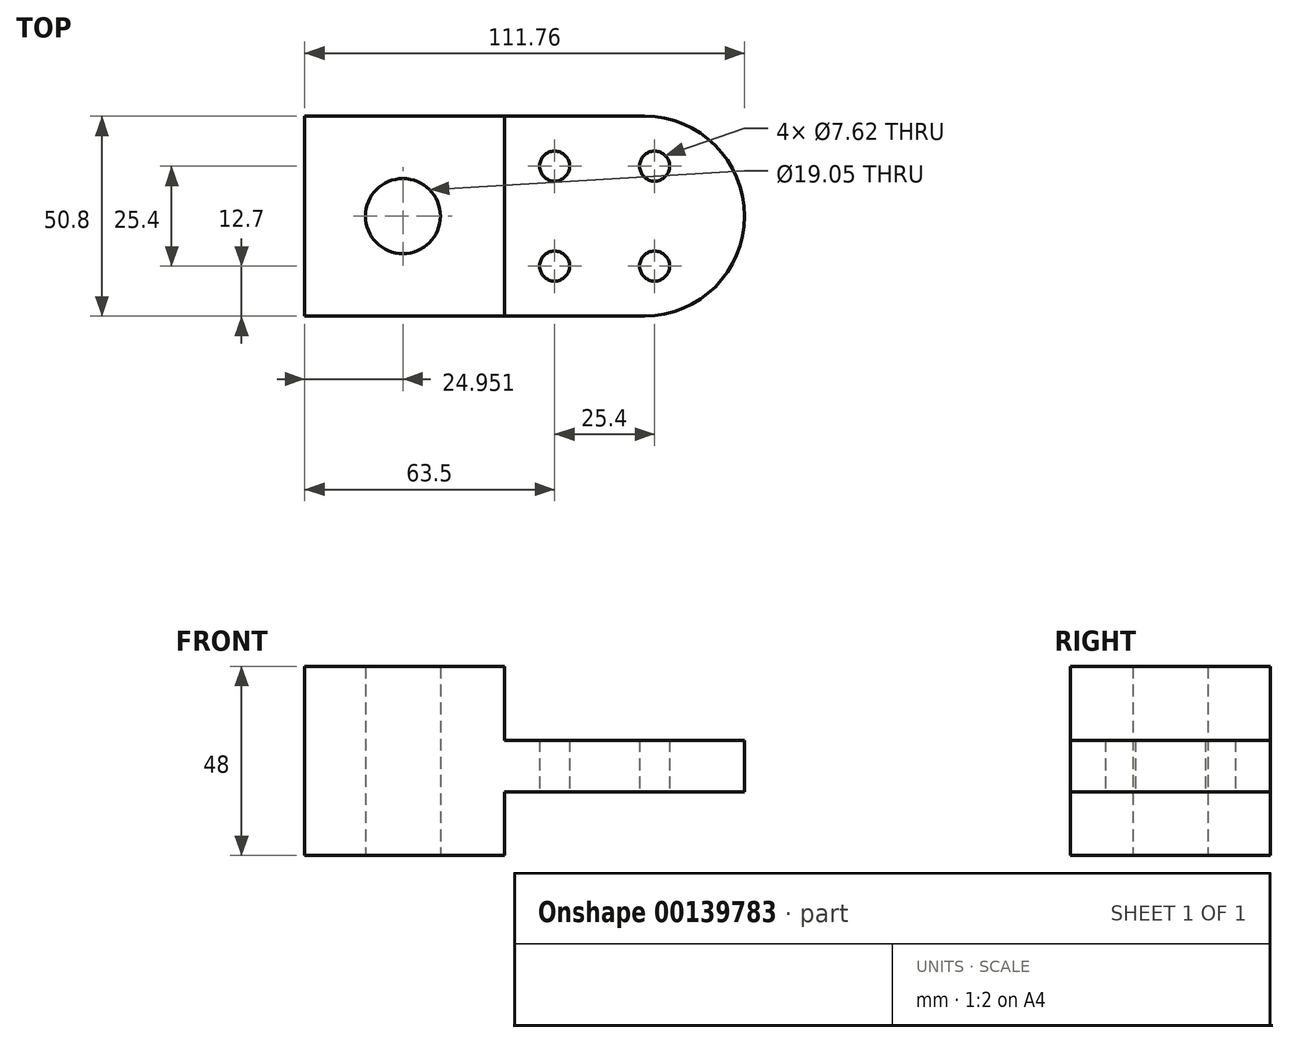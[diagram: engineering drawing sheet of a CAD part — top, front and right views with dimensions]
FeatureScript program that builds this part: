
annotation { "Feature Type Name" : "Feature", "Feature Type Description" : "" }
export const myFeature = defineFeature(function(context is Context, id is Id, definition is map)
    precondition{}
    {
        {
            var Q0;
            Q0=qCreatedBy(makeId("Front.planeOp"),FACE);
            var sketch = newSketch(context, id + "F0", { "sketchPlane" : qUnion([Q0])});
            skLineSegment(sketch, "E0", {"start": v(0, 0) * mm, "end": v(0, 48) * mm});
            skLineSegment(sketch, "E1", {"start": v(0, 48) * mm, "end": v(50.8, 48) * mm});
            skLineSegment(sketch, "E2", {"start": v(50.8, 48) * mm, "end": v(50.8, 29.23) * mm});
            skLineSegment(sketch, "E3", {"start": v(50.8, 29.23) * mm, "end": v(111.76, 29.23) * mm});
            skLineSegment(sketch, "E4", {"start": v(111.76, 29.23) * mm, "end": v(111.76, 16.07) * mm});
            skLineSegment(sketch, "E5", {"start": v(111.76, 16.07) * mm, "end": v(50.8, 16.07) * mm});
            skLineSegment(sketch, "E6", {"start": v(50.8, 16.07) * mm, "end": v(50.8, 0) * mm});
            skLineSegment(sketch, "E7", {"start": v(50.8, 0) * mm, "end": v(0, 0) * mm});
            skSolve(sketch);
        }
        {
            var Q0;
            Q0 = qSketchRegion(id + "F0", true);
            extrude(context, id + "F1", {"entities" : qUnion([Q0]), "depth" : 50.8 * mm});
        }
        {
            var Q0;
            Q0=qCreatedBy(makeId("Top.planeOp"),FACE);
            var sketch = newSketch(context, id + "F2", { "sketchPlane" : qUnion([Q0])});
            skPoint(sketch, "E8", {"position": v(24.95, -25.4) * mm});
            skCircle(sketch, "E9", {"center": v(63.5, -12.7) * mm, "radius": 3.81 * mm});
            skCircle(sketch, "E10.0.1.0", {"center": v(63.5, -38.1) * mm, "radius": 3.81 * mm});
            skLineSegment(sketch, "E10.direction1", {"start": v(63.5, -12.7) * mm, "end": v(88.9, -12.7) * mm, "construction": true});
            skLineSegment(sketch, "E10.direction2", {"start": v(63.5, -12.7) * mm, "end": v(63.5, -38.1) * mm, "construction": true});
            skCircle(sketch, "E11.0.1.0", {"center": v(88.9, -12.7) * mm, "radius": 3.81 * mm});
            skCircle(sketch, "E11.0.1.1", {"center": v(88.9, -38.1) * mm, "radius": 3.81 * mm});
            skLineSegment(sketch, "E12", {"start": v(86.36, 0) * mm, "end": v(88.9, 0) * mm});
            skLineSegment(sketch, "E13", {"start": v(111.76, -25.4) * mm, "end": v(111.76, -25.4) * mm});
            skLineSegment(sketch, "E14", {"start": v(88.9, -50.8) * mm, "end": v(86.36, -50.8) * mm});
            skPoint(sketch, "E15.visualSharp", {"position": v(111.76, 0) * mm});
            skArc(sketch, "E15.filletArc", {"start": v(111.76, -25.4) * mm, "mid": v(104.32, -7.44) * mm, "end": v(86.36, 0) * mm});
            skPoint(sketch, "E16.visualSharp", {"position": v(111.76, -50.8) * mm});
            skArc(sketch, "E16.filletArc", {"start": v(86.36, -50.8) * mm, "mid": v(104.32, -43.36) * mm, "end": v(111.76, -25.4) * mm});
            skLineSegment(sketch, "E17", {"start": v(88.9, -50.8) * mm, "end": v(111.76, -50.8) * mm});
            skLineSegment(sketch, "E18", {"start": v(111.76, 0) * mm, "end": v(88.9, 0) * mm});
            skLineSegment(sketch, "E19", {"start": v(111.76, 0) * mm, "end": v(111.76, -50.8) * mm});
            skSolve(sketch);
        }
        {
            var Q0;
            Q0=sQuery(id+"F2.wireOp",VERTEX,"E8");
            var Q1;
            Q1=makeQuery(id+"F1.opExtrude","SWEPT_BODY",BODY,{"disambiguationData":[OSD([sQuery(id+"F0.wireOp",EDGE,"E0"),sQuery(id+"F0.wireOp",EDGE,"E1"),sQuery(id+"F0.wireOp",EDGE,"E2"),sQuery(id+"F0.wireOp",EDGE,"E3"),sQuery(id+"F0.wireOp",EDGE,"E4"),sQuery(id+"F0.wireOp",EDGE,"E5"),sQuery(id+"F0.wireOp",EDGE,"E6"),sQuery(id+"F0.wireOp",EDGE,"E7")])]});
            hole(context, id + "F3", {"style" : HoleStyle.SIMPLE, "endStyle" : HoleEndStyle.THROUGH, "oppositeDirection" : true, "holeDiameter" : 19.05 * mm, "locations" : qUnion([Q0]), "scope" : qUnion([Q1]), "isTappedThrough" : true});
        }
        {
            var Q0;
            Q0 = qSketchRegion(id + "F2", true);
            extrude(context, id + "F4", {"entities" : qUnion([Q0]), "operationType" : NewBodyOperationType.REMOVE, "endBound" : BoundingType.THROUGH_ALL, "depth" : 25.4 * mm});
        }
    });
